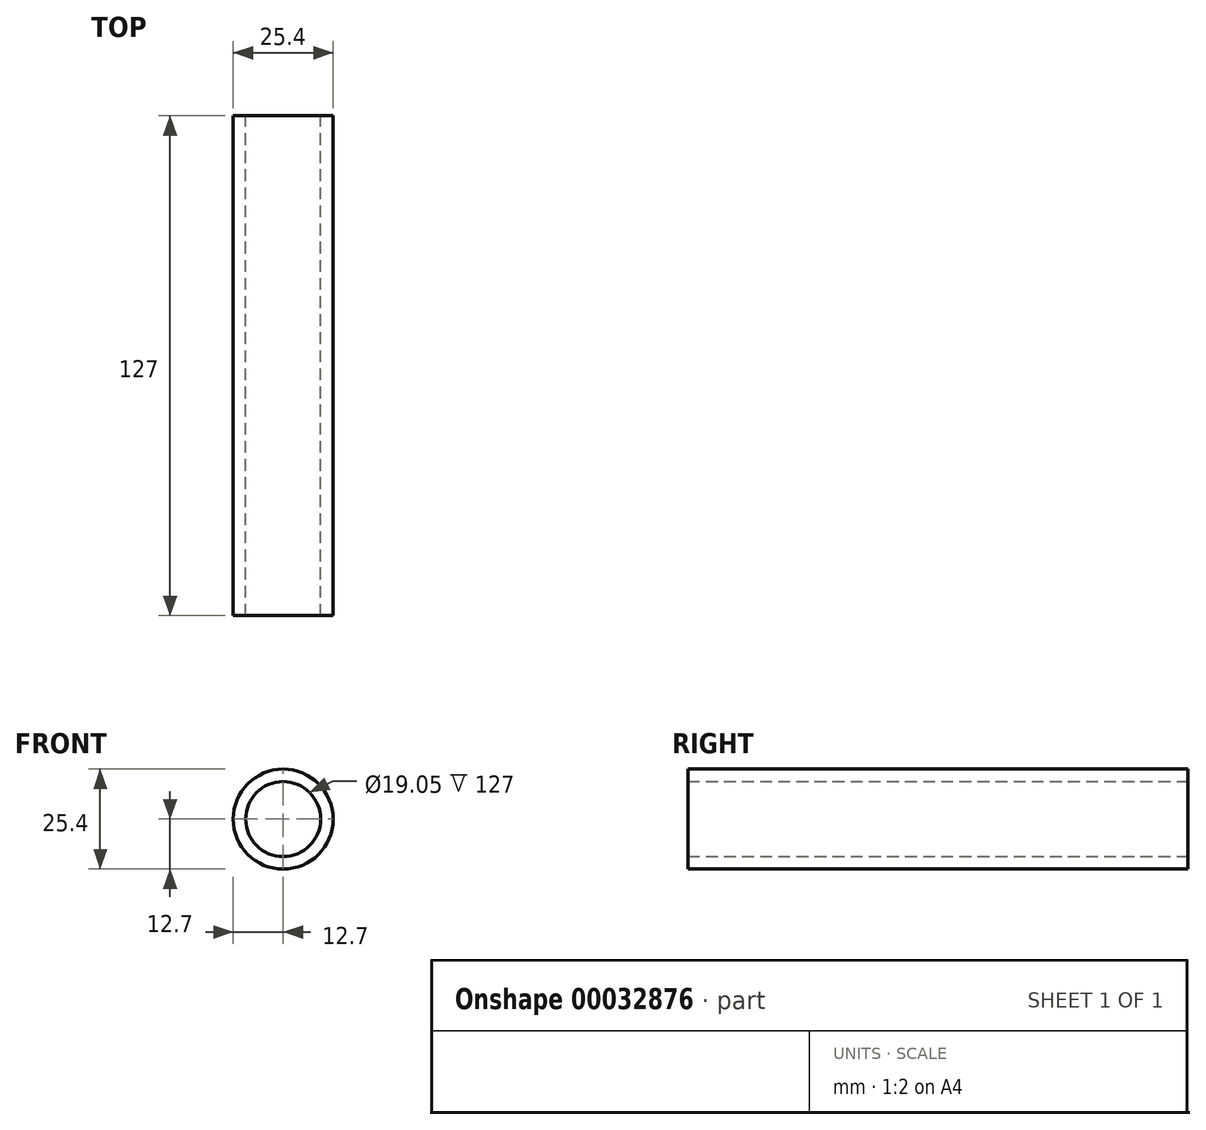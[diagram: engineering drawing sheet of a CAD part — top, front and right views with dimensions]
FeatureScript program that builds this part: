
annotation { "Feature Type Name" : "Feature", "Feature Type Description" : "" }
export const myFeature = defineFeature(function(context is Context, id is Id, definition is map)
    precondition{}
    {
        {
            var Q0;
            Q0=qCreatedBy(makeId("Front.planeOp"),FACE);
            var sketch = newSketch(context, id + "F0", { "sketchPlane" : qUnion([Q0])});
            skCircle(sketch, "E0", {"center": v(0, 0) * mm, "radius": 12.7 * mm});
            skCircle(sketch, "E1", {"center": v(0, 0) * mm, "radius": 9.53 * mm});
            skSolve(sketch);
        }
        {
            var Q0;
            Q0 = qSketchRegion(id + "F0", true);
            extrude(context, id + "F1", {"entities" : qUnion([Q0]), "depth" : 127 * mm});
        }
    });
